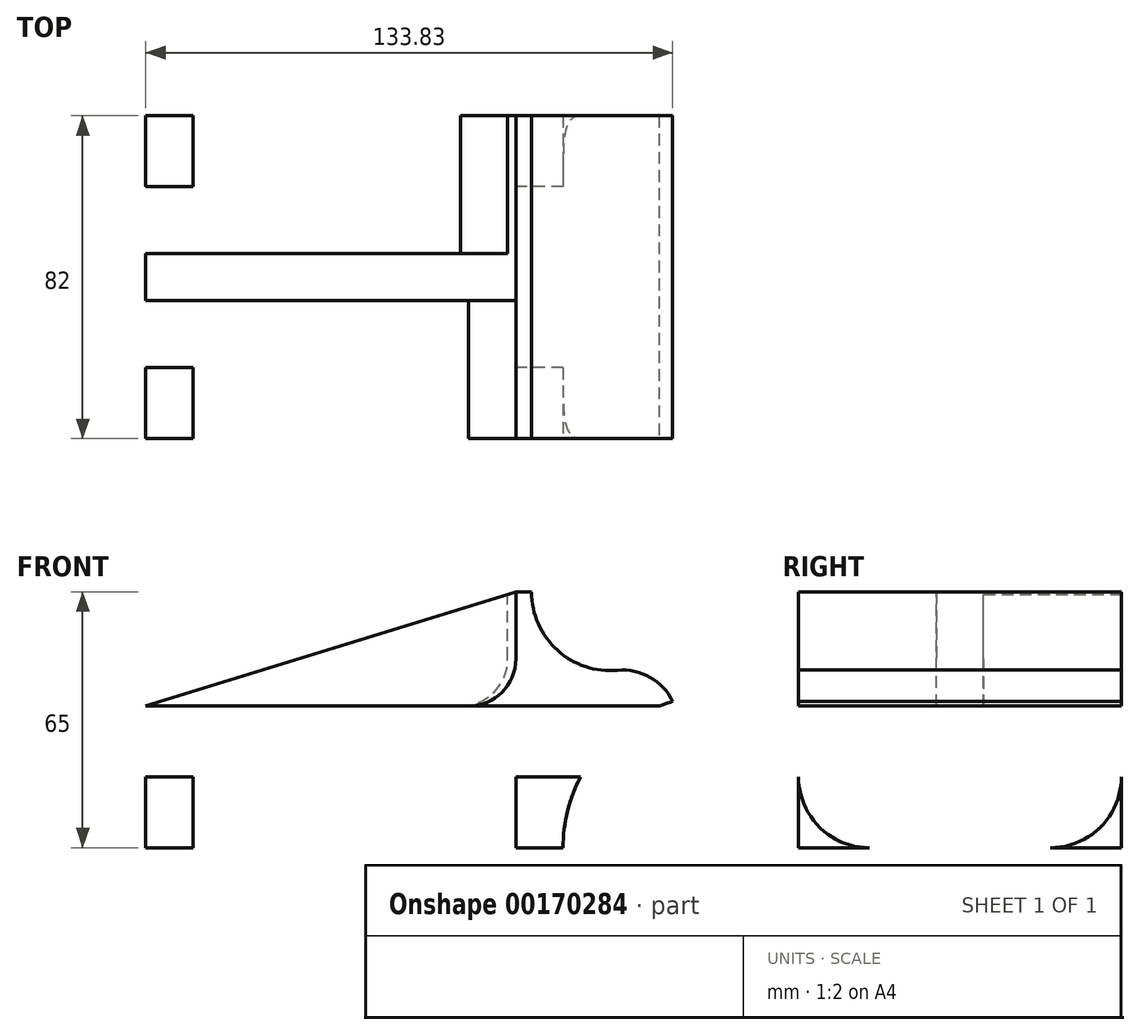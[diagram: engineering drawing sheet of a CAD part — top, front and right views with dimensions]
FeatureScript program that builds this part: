
annotation { "Feature Type Name" : "Feature", "Feature Type Description" : "" }
export const myFeature = defineFeature(function(context is Context, id is Id, definition is map)
    precondition{}
    {
        {
            var Q0;
            Q0=qCreatedBy(makeId("Front.planeOp"),FACE);
            var sketch = newSketch(context, id + "F0", { "sketchPlane" : qUnion([Q0])});
            skLineSegment(sketch, "E0.bottom", {"start": v(58.05, 0) * mm, "end": v(-91.95, 0) * mm});
            skLineSegment(sketch, "E0.top", {"start": v(58.05, 65) * mm, "end": v(-91.95, 65) * mm});
            skLineSegment(sketch, "E0.left", {"start": v(58.05, 0) * mm, "end": v(58.05, 65) * mm});
            skLineSegment(sketch, "E0.right", {"start": v(-91.95, 0) * mm, "end": v(-91.95, 65) * mm});
            skSolve(sketch);
        }
        {
            var Q0;
            Q0=makeQuery(id+"F0.imprint","IMPRINT",FACE,{"disambiguationData":[TD([[makeQuery(id+"F0.imprint","IMPRINT",EDGE,{"derivedFrom":sQuery(id+"F0.wireOp",EDGE,"E0.bottom")}),-1.0]])]});
            extrude(context, id + "F1", {"entities" : qUnion([Q0]), "depth" : 82 * mm});
        }
        {
            var Q0;
            Q0=makeQuery(id+"F1.opExtrude","CAP_FACE",FACE,{"disambiguationData":[OSD([sQuery(id+"F0.wireOp",EDGE,"E0.bottom"),sQuery(id+"F0.wireOp",EDGE,"E0.top"),sQuery(id+"F0.wireOp",EDGE,"E0.left"),sQuery(id+"F0.wireOp",EDGE,"E0.right")])],"isStart":false});
            var sketch = newSketch(context, id + "F10", { "sketchPlane" : qUnion([Q0])});
            skLineSegment(sketch, "E1.bottom", {"start": v(-79.95, 0) * mm, "end": v(2.05, 0) * mm});
            skLineSegment(sketch, "E1.top", {"start": v(-79.95, 24) * mm, "end": v(2.05, 24) * mm});
            skLineSegment(sketch, "E1.left", {"start": v(-79.95, 0) * mm, "end": v(-79.95, 24) * mm});
            skLineSegment(sketch, "E1.right", {"start": v(2.05, 0) * mm, "end": v(2.05, 24) * mm});
            skArc(sketch, "E2", {"start": v(40.9, 43.54) * mm, "mid": v(38.68, 43.36) * mm, "end": v(36.48, 43) * mm});
            skLineSegment(sketch, "E3", {"start": v(14.05, 0) * mm, "end": v(14.05, 44.74) * mm});
            skPoint(sketch, "E4.orphan", {"position": v(58.05, 65) * mm});
            skCircle(sketch, "E5", {"center": v(26.05, 65) * mm, "radius": 20 * mm});
            skArc(sketch, "E6", {"start": v(20, 20.64) * mm, "mid": v(42.56, 26.83) * mm, "end": v(27.93, 45.09) * mm});
            skArc(sketch, "E7", {"start": v(58.05, 65) * mm, "mid": v(53.72, 48.91) * mm, "end": v(41.88, 37.19) * mm});
            skArc(sketch, "E8", {"start": v(41.88, 37.19) * mm, "mid": v(21.78, 23.22) * mm, "end": v(14.05, 0) * mm});
            skSolve(sketch);
        }
        {
            var Q0;
            {var subQ4=makeQuery(id+"F1.opExtrude","CAP_EDGE",EDGE,{"disambiguationData":[OSD([sQuery(id+"F0.wireOp",EDGE,"E0.left")])],"isStart":false});Q0=makeQuery(id+"F10.imprint","IMPRINT",FACE,{"disambiguationData":[TD([[makeQuery(id+"F10.imprint","IMPRINT",EDGE,{"derivedFrom":subQ4}),1.0]])]});}
            var Q1;
            {var subQ0=sQuery(id+"F10.wireOp",EDGE,"E2");var subQ1=makeQuery(id+"F1.opExtrude","CAP_EDGE",EDGE,{"disambiguationData":[OSD([sQuery(id+"F0.wireOp",EDGE,"E0.bottom")])],"isStart":false});var subQ2=makeQuery(id+"F10.imprint","INTERSECT",VERTEX,{"derivedFrom":[subQ1,subQ0]});Q1=makeQuery(id+"F10.imprint","IMPRINT",FACE,{"disambiguationData":[TD([[makeQuery(id+"F10.imprint","IMPRINT",EDGE,{"disambiguationData":[TD([[subQ2,1.0]])],"derivedFrom":subQ0}),-1.0]])]});}
            var Q2;
            Q2=makeQuery(id+"F10.imprint","IMPRINT",FACE,{"disambiguationData":[TD([[makeQuery(id+"F10.imprint","IMPRINT",EDGE,{"derivedFrom":sQuery(id+"F10.wireOp",EDGE,"E1.bottom")}),-1.0]])]});
            var Q3;
            {var subQ0=sQuery(id+"F10.wireOp",EDGE,"345b6d2b-691e-4165-82f6-7e63cc16f6b3");var subQ1=makeQuery(id+"F1.opExtrude","CAP_EDGE",EDGE,{"disambiguationData":[OSD([sQuery(id+"F0.wireOp",EDGE,"E0.top")])],"isStart":false});var subQ2=makeQuery(id+"F10.imprint","INTERSECT",VERTEX,{"disambiguationData":[OD(0.0)],"derivedFrom":[subQ1,subQ0]});Q3=makeQuery(id+"F10.imprint","IMPRINT",FACE,{"disambiguationData":[TD([[makeQuery(id+"F10.imprint","IMPRINT",EDGE,{"disambiguationData":[TD([[subQ2,1.0]])],"derivedFrom":subQ0}),1.0]])]});}
            extrude(context, id + "F2", {"entities" : qUnion([Q0, Q1, Q2, Q3]), "operationType" : NewBodyOperationType.REMOVE, "oppositeDirection" : true, "depth" : 82 * mm});
        }
        {
            var Q0;
            Q0=makeQuery(id+"F1.opExtrude","CAP_FACE",FACE,{"disambiguationData":[OSD([sQuery(id+"F0.wireOp",EDGE,"E0.bottom"),sQuery(id+"F0.wireOp",EDGE,"E0.top"),sQuery(id+"F0.wireOp",EDGE,"E0.left"),sQuery(id+"F0.wireOp",EDGE,"E0.right")])],"isStart":false});
            var sketch = newSketch(context, id + "F11", { "sketchPlane" : qUnion([Q0])});
            skLineSegment(sketch, "E9", {"start": v(2.05, 65) * mm, "end": v(2.05, 48) * mm});
            skLineSegment(sketch, "E10", {"start": v(-91.95, 36) * mm, "end": v(-9.95, 36) * mm});
            skPoint(sketch, "E11.visualSharp", {"position": v(2.05, 36) * mm});
            skArc(sketch, "E11.filletArc", {"start": v(-9.95, 36) * mm, "mid": v(-1.46, 39.51) * mm, "end": v(2.05, 48) * mm});
            skLineSegment(sketch, "E12", {"start": v(-91.95, 36) * mm, "end": v(2.05, 65) * mm});
            skSolve(sketch);
        }
        {
            var Q0;
            {var subQ0=sQuery(id+"F11.wireOp",EDGE,"E12");Q0=makeQuery(id+"F11.imprint","IMPRINT",FACE,{"disambiguationData":[TD([[makeQuery(id+"F11.imprint","IMPRINT",EDGE,{"derivedFrom":subQ0}),1.0]])]});}
            extrude(context, id + "F3", {"entities" : qUnion([Q0]), "operationType" : NewBodyOperationType.REMOVE, "oppositeDirection" : true, "depth" : 82 * mm});
        }
        {
            var Q0;
            {var subQ0=sQuery(id+"F11.wireOp",EDGE,"E12");Q0=makeQuery(id+"F11.imprint","IMPRINT",FACE,{"disambiguationData":[TD([[makeQuery(id+"F11.imprint","IMPRINT",EDGE,{"derivedFrom":subQ0}),1.0]])]});}
            extrude(context, id + "F4", {"entities" : qUnion([Q0]), "operationType" : NewBodyOperationType.REMOVE, "oppositeDirection" : true, "depth" : 82 * mm});
        }
        {
            var Q0;
            Q0=makeQuery(id+"F11.imprint","IMPRINT",FACE,{"disambiguationData":[TD([[makeQuery(id+"F11.imprint","IMPRINT",EDGE,{"derivedFrom":sQuery(id+"F11.wireOp",EDGE,"E9")}),-1.0]])]});
            extrude(context, id + "F5", {"entities" : qUnion([Q0]), "operationType" : NewBodyOperationType.REMOVE, "oppositeDirection" : true, "depth" : 35 * mm});
        }
        {
            var Q0;
            Q0=makeQuery(id+"F1.opExtrude","CAP_FACE",FACE,{"disambiguationData":[OSD([sQuery(id+"F0.wireOp",EDGE,"E0.bottom"),sQuery(id+"F0.wireOp",EDGE,"E0.top"),sQuery(id+"F0.wireOp",EDGE,"E0.left"),sQuery(id+"F0.wireOp",EDGE,"E0.right")])],"isStart":true});
            var sketch = newSketch(context, id + "F6", { "sketchPlane" : qUnion([Q0])});
            skLineSegment(sketch, "E13", {"start": v(91.95, 36) * mm, "end": v(12, 36) * mm});
            skLineSegment(sketch, "E14", {"start": v(0, 48) * mm, "end": v(0, 66.58) * mm});
            skPoint(sketch, "E15.visualSharp", {"position": v(0, 36) * mm});
            skArc(sketch, "E15.filletArc", {"start": v(0, 48) * mm, "mid": v(3.51, 39.51) * mm, "end": v(12, 36) * mm});
            skSolve(sketch);
        }
        {
            var Q0;
            {var subQ0=sQuery(id+"F6.wireOp",EDGE,"E13");Q0=makeQuery(id+"F6.imprint","IMPRINT",FACE,{"disambiguationData":[TD([[makeQuery(id+"F6.imprint","IMPRINT",EDGE,{"derivedFrom":subQ0}),-1.0]])]});}
            extrude(context, id + "F7", {"entities" : qUnion([Q0]), "operationType" : NewBodyOperationType.REMOVE, "oppositeDirection" : true, "depth" : 35 * mm});
        }
        {
            var Q0;
            Q0=makeQuery(id+"F1.opExtrude","SWEPT_FACE",FACE,{"disambiguationData":[OSD([sQuery(id+"F0.wireOp",EDGE,"E0.right")])]});
            var sketch = newSketch(context, id + "F8", { "sketchPlane" : qUnion([Q0])});
            skCircle(sketch, "E16", {"center": v(64, 18) * mm, "radius": 6 * mm});
            skCircle(sketch, "E17", {"center": v(18, 18) * mm, "radius": 6 * mm});
            skArc(sketch, "E18", {"start": v(18, 0) * mm, "mid": v(5.27, 5.27) * mm, "end": v(0, 18) * mm});
            skArc(sketch, "E19", {"start": v(82, 18) * mm, "mid": v(76.73, 5.27) * mm, "end": v(64, 0) * mm});
            skSolve(sketch);
        }
        {
            var Q0;
            Q0=makeQuery(id+"F8.imprint","IMPRINT",FACE,{"disambiguationData":[TD([[makeQuery(id+"F8.imprint","IMPRINT",EDGE,{"derivedFrom":sQuery(id+"F8.wireOp",EDGE,"E16")}),-1.0]])]});
            var sketch = newSketch(context, id + "F12", { "sketchPlane" : qUnion([Q0])});
            skSolve(sketch);
        }
        {
            var Q0;
            Q0=makeQuery(id+"F8.imprint","IMPRINT",FACE,{"disambiguationData":[TD([[makeQuery(id+"F8.imprint","IMPRINT",EDGE,{"derivedFrom":sQuery(id+"F8.wireOp",EDGE,"E17")}),1.0]])]});
            var Q1;
            Q1=makeQuery(id+"F8.imprint","IMPRINT",FACE,{"disambiguationData":[TD([[makeQuery(id+"F8.imprint","IMPRINT",EDGE,{"derivedFrom":sQuery(id+"F8.wireOp",EDGE,"E16")}),1.0]])]});
            var Q2;
            Q2=makeQuery(id+"F12.imprint","IMPRINT",FACE,{"disambiguationData":[TD([[makeQuery(id+"F12.imprint","IMPRINT",EDGE,{"derivedFrom":makeQuery(id+"F8.imprint","IMPRINT",EDGE,{"derivedFrom":sQuery(id+"F8.wireOp",EDGE,"E17")})}),1.0]])]});
            extrude(context, id + "F13", {"entities" : qUnion([Q0, Q1, Q2]), "operationType" : NewBodyOperationType.REMOVE, "oppositeDirection" : true, "depth" : 150 * mm});
        }
        {
            var Q0;
            {var subQ0=sQuery(id+"F8.wireOp",EDGE,"E18");Q0=makeQuery(id+"F8.imprint","IMPRINT",FACE,{"disambiguationData":[TD([[makeQuery(id+"F8.imprint","IMPRINT",EDGE,{"derivedFrom":subQ0}),1.0]])]});}
            var Q1;
            {var subQ0=sQuery(id+"F8.wireOp",EDGE,"E19");Q1=makeQuery(id+"F8.imprint","IMPRINT",FACE,{"disambiguationData":[TD([[makeQuery(id+"F8.imprint","IMPRINT",EDGE,{"derivedFrom":subQ0}),1.0]])]});}
            extrude(context, id + "F14", {"entities" : qUnion([Q0, Q1]), "operationType" : NewBodyOperationType.REMOVE, "oppositeDirection" : true, "depth" : 150 * mm});
        }
        {
            var Q0;
            {var subQ0=sQuery(id+"F10.wireOp",EDGE,"E8");var subQ1=sQuery(id+"F10.wireOp",EDGE,"E6");var subQ2=makeQuery(id+"F10.imprint","INTERSECT",VERTEX,{"derivedFrom":[subQ1,subQ0]});Q0=makeQuery(id+"F10.imprint","IMPRINT",FACE,{"disambiguationData":[TD([[makeQuery(id+"F10.imprint","IMPRINT",EDGE,{"disambiguationData":[TD([[subQ2,-1.0]])],"derivedFrom":subQ1}),1.0]])]});}
            var Q1;
            {var subQ0=sQuery(id+"F10.wireOp",EDGE,"E7");Q1=makeQuery(id+"F10.imprint","IMPRINT",FACE,{"disambiguationData":[TD([[makeQuery(id+"F10.imprint","IMPRINT",EDGE,{"derivedFrom":subQ0}),1.0]])]});}
            var Q2;
            {var subQ0=sQuery(id+"F10.wireOp",EDGE,"E5");var subQ1=makeQuery(id+"F10.imprint","INTERSECT",VERTEX,{"derivedFrom":[subQ0,sQuery(id+"F10.wireOp",EDGE,"E6")]});Q2=makeQuery(id+"F10.imprint","IMPRINT",FACE,{"disambiguationData":[TD([[makeQuery(id+"F10.imprint","IMPRINT",EDGE,{"disambiguationData":[TD([[subQ1,1.0]])],"derivedFrom":subQ0}),1.0]])]});}
            extrude(context, id + "F9", {"entities" : qUnion([Q0, Q1, Q2]), "operationType" : NewBodyOperationType.REMOVE, "oppositeDirection" : true, "depth" : 82 * mm});
        }
    });
